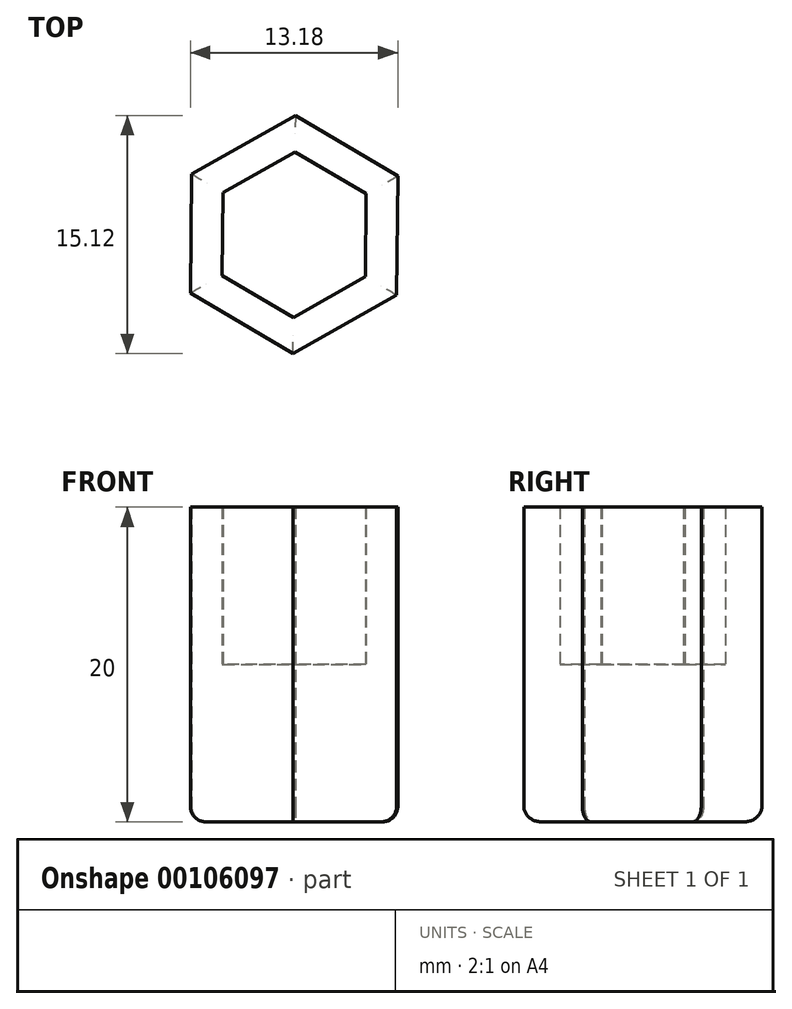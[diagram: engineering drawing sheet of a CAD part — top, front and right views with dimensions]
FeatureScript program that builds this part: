
annotation { "Feature Type Name" : "Feature", "Feature Type Description" : "" }
export const myFeature = defineFeature(function(context is Context, id is Id, definition is map)
    precondition{}
    {
        {
            var Q0;
            Q0=qCreatedBy(makeId("Top.planeOp"),FACE);
            var sketch = newSketch(context, id + "F0", { "sketchPlane" : qUnion([Q0])});
            skCircle(sketch, "E0.cCircle", {"center": v(0, 0) * mm, "radius": 4.55 * mm, "construction": true});
            skLineSegment(sketch, "E0.0", {"start": v(0.04, 5.25) * mm, "end": v(4.57, 2.59) * mm});
            skLineSegment(sketch, "E0.1", {"start": v(4.57, 2.59) * mm, "end": v(4.53, -2.66) * mm});
            skLineSegment(sketch, "E0.2", {"start": v(4.53, -2.66) * mm, "end": v(-0.04, -5.25) * mm});
            skLineSegment(sketch, "E0.3", {"start": v(-0.04, -5.25) * mm, "end": v(-4.57, -2.59) * mm});
            skLineSegment(sketch, "E0.4", {"start": v(-4.57, -2.59) * mm, "end": v(-4.53, 2.66) * mm});
            skLineSegment(sketch, "E0.5", {"start": v(-4.53, 2.66) * mm, "end": v(0.04, 5.25) * mm});
            skPoint(sketch, "E0.0.midPoint", {"position": v(2.3, 3.92) * mm});
            skCircle(sketch, "E1.cCircle", {"center": v(0, 0) * mm, "radius": 6.55 * mm, "construction": true});
            skLineSegment(sketch, "E1.0", {"start": v(0.08, 7.56) * mm, "end": v(6.59, 3.71) * mm});
            skLineSegment(sketch, "E1.1", {"start": v(6.59, 3.71) * mm, "end": v(6.51, -3.85) * mm});
            skLineSegment(sketch, "E1.2", {"start": v(6.51, -3.85) * mm, "end": v(-0.08, -7.56) * mm});
            skLineSegment(sketch, "E1.3", {"start": v(-0.08, -7.56) * mm, "end": v(-6.59, -3.71) * mm});
            skLineSegment(sketch, "E1.4", {"start": v(-6.59, -3.71) * mm, "end": v(-6.51, 3.85) * mm});
            skLineSegment(sketch, "E1.5", {"start": v(-6.51, 3.85) * mm, "end": v(0.08, 7.56) * mm});
            skPoint(sketch, "E1.0.midPoint", {"position": v(3.33, 5.64) * mm});
            skLineSegment(sketch, "E2", {"start": v(0.04, 5.25) * mm, "end": v(-0.04, -5.25) * mm, "construction": true});
            skLineSegment(sketch, "E3", {"start": v(-4.57, -2.59) * mm, "end": v(4.53, -2.66) * mm, "construction": true});
            skLineSegment(sketch, "E4", {"start": v(-4.55, 0) * mm, "end": v(-6.55, 0.02) * mm, "construction": true});
            skSolve(sketch);
        }
        {
            var Q0;
            Q0=makeQuery(id+"F0.imprint","IMPRINT",FACE,{"disambiguationData":[TD([[makeQuery(id+"F0.imprint","IMPRINT",EDGE,{"derivedFrom":sQuery(id+"F0.wireOp",EDGE,"E0.0")}),-1.0]])]});
            extrude(context, id + "F1", {"entities" : qUnion([Q0]), "depth" : 10 * mm, "offsetDistance" : 25 * mm});
        }
        {
            var Q0;
            Q0=makeQuery(id+"F0.imprint","IMPRINT",FACE,{"disambiguationData":[TD([[makeQuery(id+"F0.imprint","IMPRINT",EDGE,{"derivedFrom":sQuery(id+"F0.wireOp",EDGE,"E0.0")}),1.0]])]});
            extrude(context, id + "F2", {"entities" : qUnion([Q0]), "operationType" : NewBodyOperationType.ADD, "depth" : 20 * mm, "offsetDistance" : 25 * mm});
        }
        {
            var Q0;
            Q0=makeQuery(id+"F2.opExtrude","CAP_EDGE",EDGE,{"disambiguationData":[OSD([sQuery(id+"F0.wireOp",EDGE,"E1.2")])],"isStart":true});
            var Q1;
            Q1=makeQuery(id+"F2.opExtrude","CAP_EDGE",EDGE,{"disambiguationData":[OSD([sQuery(id+"F0.wireOp",EDGE,"E1.3")])],"isStart":true});
            var Q2;
            Q2=makeQuery(id+"F2.opExtrude","CAP_EDGE",EDGE,{"disambiguationData":[OSD([sQuery(id+"F0.wireOp",EDGE,"E1.4")])],"isStart":true});
            var Q3;
            Q3=makeQuery(id+"F2.opExtrude","CAP_EDGE",EDGE,{"disambiguationData":[OSD([sQuery(id+"F0.wireOp",EDGE,"E1.5")])],"isStart":true});
            var Q4;
            Q4=makeQuery(id+"F2.opExtrude","CAP_EDGE",EDGE,{"disambiguationData":[OSD([sQuery(id+"F0.wireOp",EDGE,"E1.0")])],"isStart":true});
            var Q5;
            Q5=makeQuery(id+"F2.opExtrude","CAP_EDGE",EDGE,{"disambiguationData":[OSD([sQuery(id+"F0.wireOp",EDGE,"E1.1")])],"isStart":true});
            fillet(context, id + "F3", {"entities" : qUnion([Q0, Q1, Q2, Q3, Q4, Q5]), "radius" : 1 * mm, "tangentPropagation" : true, "allowEdgeOverflow" : false});
        }
    });
